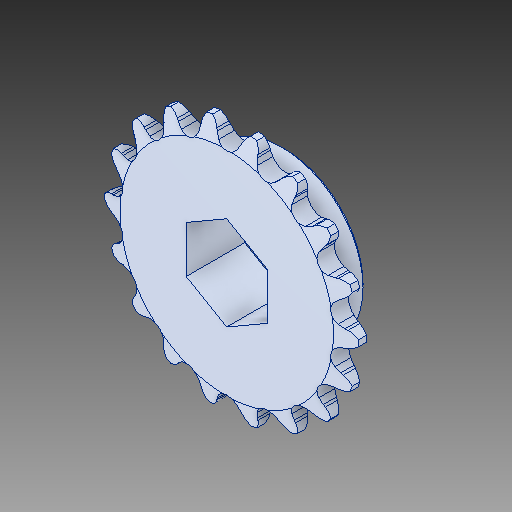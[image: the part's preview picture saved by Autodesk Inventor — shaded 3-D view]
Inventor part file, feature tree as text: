
AUTODESK INVENTOR PART (.ipt)
format: ipt  version: 2018 (Build 220112000, 112)  size: 575,488 bytes
history: native  units: in
note: dims shown in document units (in); Inventor stores cm internally (conversion verified against a paired STEP export)
features: chamfer x1
ambient origin geometry x8: Origin, YZ Plane, XZ Plane, XY Plane, X Axis, Y Axis, Z Axis, Center Point
bodies: Solid1 (feature_tree)
feature tree (1):
  chamfer  "Chamfer2"  [1 undecoded]
note: 1 required parameter value undecoded (feature->parameter linkage not recoverable at this tier; creation-order binding heuristic only, values carry confidence <= 0.55)
